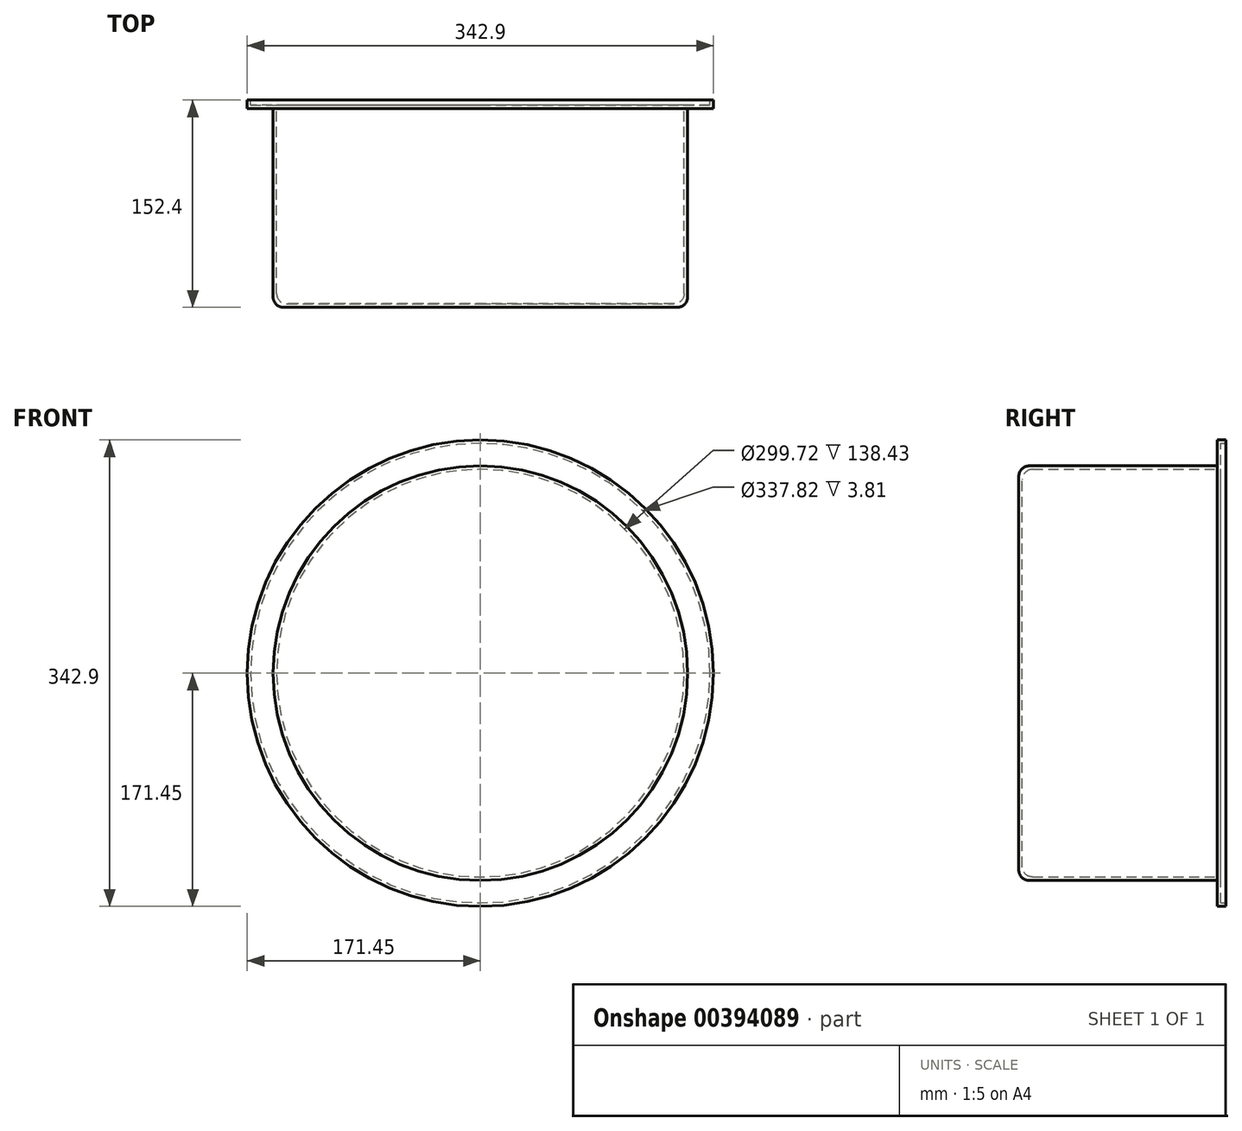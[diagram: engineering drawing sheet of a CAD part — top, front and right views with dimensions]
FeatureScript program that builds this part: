
annotation { "Feature Type Name" : "Feature", "Feature Type Description" : "" }
export const myFeature = defineFeature(function(context is Context, id is Id, definition is map)
    precondition{}
    {
        {
            var Q0;
            Q0=qCreatedBy(makeId("Front.planeOp"),FACE);
            var sketch = newSketch(context, id + "F0", { "sketchPlane" : qUnion([Q0])});
            skCircle(sketch, "E0", {"center": v(0, 0) * mm, "radius": 152.4 * mm});
            skCircle(sketch, "E1", {"center": v(0, 0) * mm, "radius": 171.45 * mm});
            skSolve(sketch);
        }
        {
            var Q0;
            Q0=makeQuery(id+"F0.imprint","IMPRINT",FACE,{"disambiguationData":[TD([[makeQuery(id+"F0.imprint","IMPRINT",EDGE,{"derivedFrom":sQuery(id+"F0.wireOp",EDGE,"E0")}),1.0]])]});
            extrude(context, id + "F1", {"entities" : qUnion([Q0]), "depth" : 152.4 * mm});
        }
        {
            var Q0;
            Q0=makeQuery(id+"F0.imprint","IMPRINT",FACE,{"disambiguationData":[TD([[makeQuery(id+"F0.imprint","IMPRINT",EDGE,{"derivedFrom":sQuery(id+"F0.wireOp",EDGE,"E0")}),-1.0]])]});
            extrude(context, id + "F2", {"entities" : qUnion([Q0]), "operationType" : NewBodyOperationType.ADD, "depth" : 6.35 * mm});
        }
        {
            var Q0;
            {var subQ0=sQuery(id+"F0.wireOp",EDGE,"E0");Q0=makeQuery(id+"F2.boolean.opBoolean","MERGE",FACE,{"derivedFrom":[makeQuery(id+"F1.opExtrude","CAP_FACE",FACE,{"disambiguationData":[OSD([subQ0])],"isStart":true}),makeQuery(id+"F2.opExtrude","CAP_FACE",FACE,{"disambiguationData":[OSD([subQ0,sQuery(id+"F0.wireOp",EDGE,"E1")])],"isStart":true})]});}
            shell(context, id + "F3", {"entities" : qUnion([Q0]), "thickness" : 2.54 * mm});
        }
        {
            var Q0;
            Q0=makeQuery(id+"F1.opExtrude","CAP_EDGE",EDGE,{"disambiguationData":[OSD([sQuery(id+"F0.wireOp",EDGE,"E0")])],"isStart":false});
            var Q1;
            Q1=makeQuery(id+"F2.opExtrude","CAP_EDGE",EDGE,{"disambiguationData":[OSD([sQuery(id+"F0.wireOp",EDGE,"E0")])],"isStart":false});
            var Q2;
            {var subQ0=sQuery(id+"F0.wireOp",EDGE,"E0");Q2=makeQuery(id+"F3.opShell","OFFSET_EDGE",EDGE,{"disambiguationData":[OSD([subQ0]),TDD([makeQuery(id+"F1.opExtrude","CAP_EDGE",EDGE,{"disambiguationData":[OSD([subQ0])],"isStart":false})])]});}
            fillet(context, id + "F4", {"entities" : qUnion([Q0, Q1, Q2]), "radius" : 7.62 * mm, "tangentPropagation" : true, "allowEdgeOverflow" : false});
        }
    });
